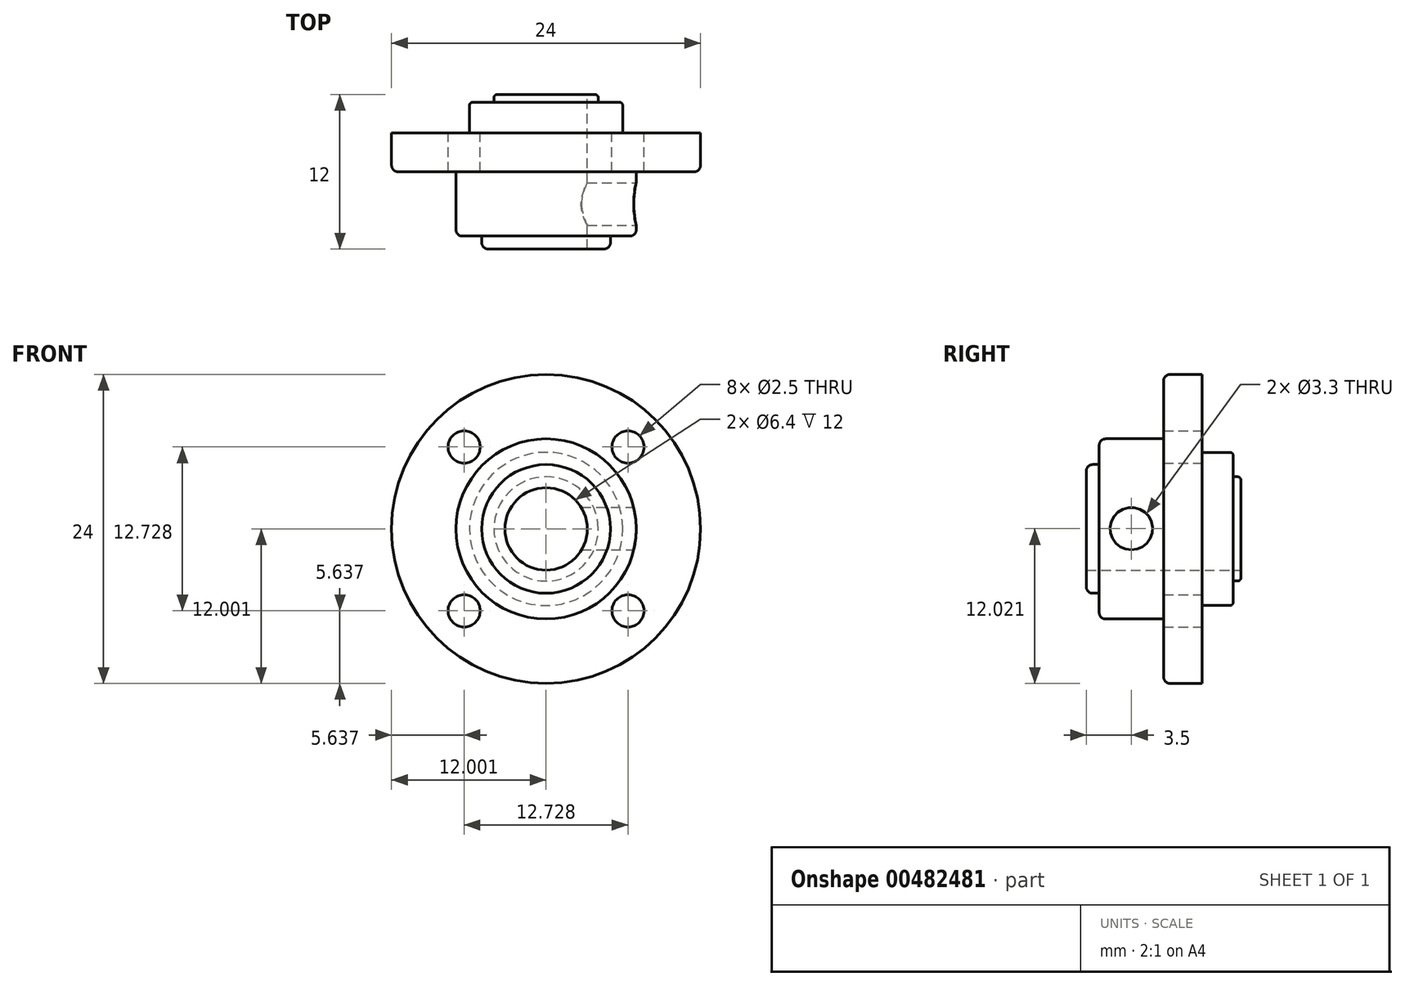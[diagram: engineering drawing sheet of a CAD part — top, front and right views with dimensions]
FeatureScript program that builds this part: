
annotation { "Feature Type Name" : "Feature", "Feature Type Description" : "" }
export const myFeature = defineFeature(function(context is Context, id is Id, definition is map)
    precondition{}
    {
        {
            var Q0;
            Q0=qCreatedBy(makeId("Front.planeOp"),FACE);
            var sketch = newSketch(context, id + "F0", { "sketchPlane" : qUnion([Q0])});
            skCircle(sketch, "E0", {"center": v(-51.93, 29.55) * mm, "radius": 5.95 * mm});
            skCircle(sketch, "E1", {"center": v(-51.93, 29.55) * mm, "radius": 12 * mm});
            skCircle(sketch, "E2", {"center": v(-51.93, 29.55) * mm, "radius": 3.2 * mm});
            skCircle(sketch, "E3", {"center": v(-58.3, 35.91) * mm, "radius": 1.25 * mm});
            skCircle(sketch, "E4", {"center": v(-45.57, 35.91) * mm, "radius": 1.25 * mm});
            skCircle(sketch, "E5", {"center": v(-45.57, 23.19) * mm, "radius": 1.25 * mm});
            skCircle(sketch, "E6", {"center": v(-58.3, 23.19) * mm, "radius": 1.25 * mm});
            skSolve(sketch);
        }
        {
            var Q0;
            Q0 = qSketchRegion(id + "F0", true);
            var Q1;
            Q1=makeQuery(id+"F0.imprint","IMPRINT",FACE,{"disambiguationData":[TD([[makeQuery(id+"F0.imprint","IMPRINT",EDGE,{"derivedFrom":sQuery(id+"F0.wireOp",EDGE,"E0")}),1.0]])]});
            extrude(context, id + "F1", {"entities" : qUnion([Q0, Q1]), "depth" : 3 * mm, "offsetDistance" : 25 * mm});
        }
        {
            var Q0;
            Q0=makeQuery(id+"F1.opExtrude","CAP_FACE",FACE,{"disambiguationData":[OSD([sQuery(id+"F0.wireOp",EDGE,"E1"),sQuery(id+"F0.wireOp",EDGE,"EYXUTqH9-eEcY-GaFt-dMka-iERJke81kBaa"),sQuery(id+"F0.wireOp",EDGE,"KlKgwLJu-OTFO-AsjK-VSUq-wluYezLKTBxm"),sQuery(id+"F0.wireOp",EDGE,"UiC2e6AT-jG4o-S1pj-5Rfj-m6z0H2r1u7PO"),sQuery(id+"F0.wireOp",EDGE,"hBQAIbmH-Tyc7-gpv5-7lbM-7KSF0jIbfKj2"),sQuery(id+"F0.wireOp",EDGE,"E2")])],"isStart":true});
            var sketch = newSketch(context, id + "F2", { "sketchPlane" : qUnion([Q0])});
            skCircle(sketch, "E7", {"center": v(51.93, 29.55) * mm, "radius": 5.95 * mm});
            skSolve(sketch);
        }
        {
            var Q0;
            Q0=makeQuery(id+"F2.imprint","IMPRINT",FACE,{"disambiguationData":[TD([[makeQuery(id+"F2.imprint","IMPRINT",EDGE,{"derivedFrom":sQuery(id+"F2.wireOp",EDGE,"E7")}),1.0]])]});
            extrude(context, id + "F3", {"entities" : qUnion([Q0]), "operationType" : NewBodyOperationType.ADD, "depth" : 2.4 * mm, "offsetDistance" : 25 * mm});
        }
        {
            var Q0;
            Q0=makeQuery(id+"F3.opExtrude","CAP_FACE",FACE,{"disambiguationData":[OSD([sQuery(id+"F0.wireOp",EDGE,"E2"),sQuery(id+"F2.wireOp",EDGE,"E7")])],"isStart":false});
            var sketch = newSketch(context, id + "F4", { "sketchPlane" : qUnion([Q0])});
            skCircle(sketch, "E8", {"center": v(51.93, 29.55) * mm, "radius": 4.05 * mm});
            skSolve(sketch);
        }
        {
            var Q0;
            Q0=makeQuery(id+"F4.imprint","IMPRINT",FACE,{"disambiguationData":[TD([[makeQuery(id+"F4.imprint","IMPRINT",EDGE,{"derivedFrom":sQuery(id+"F4.wireOp",EDGE,"E8")}),1.0]])]});
            extrude(context, id + "F5", {"entities" : qUnion([Q0]), "operationType" : NewBodyOperationType.ADD, "depth" : .6 * mm, "offsetDistance" : 25 * mm});
        }
        {
            var Q0;
            Q0=makeQuery(id+"F1.opExtrude","CAP_FACE",FACE,{"disambiguationData":[OSD([sQuery(id+"F0.wireOp",EDGE,"E1"),sQuery(id+"F0.wireOp",EDGE,"EYXUTqH9-eEcY-GaFt-dMka-iERJke81kBaa"),sQuery(id+"F0.wireOp",EDGE,"KlKgwLJu-OTFO-AsjK-VSUq-wluYezLKTBxm"),sQuery(id+"F0.wireOp",EDGE,"UiC2e6AT-jG4o-S1pj-5Rfj-m6z0H2r1u7PO"),sQuery(id+"F0.wireOp",EDGE,"hBQAIbmH-Tyc7-gpv5-7lbM-7KSF0jIbfKj2"),sQuery(id+"F0.wireOp",EDGE,"E2")])],"isStart":false});
            var sketch = newSketch(context, id + "F6", { "sketchPlane" : qUnion([Q0])});
            skCircle(sketch, "E9", {"center": v(-51.93, 29.55) * mm, "radius": 7 * mm});
            skSolve(sketch);
        }
        {
            var Q0;
            Q0=makeQuery(id+"F6.imprint","IMPRINT",FACE,{"disambiguationData":[TD([[makeQuery(id+"F6.imprint","IMPRINT",EDGE,{"derivedFrom":makeQuery(id+"F1.opExtrude","CAP_EDGE",EDGE,{"disambiguationData":[OSD([sQuery(id+"F0.wireOp",EDGE,"E2")])],"isStart":false})}),-1.0]])]});
            extrude(context, id + "F7", {"entities" : qUnion([Q0]), "operationType" : NewBodyOperationType.ADD, "depth" : 5 * mm, "offsetDistance" : 25 * mm});
        }
        {
            var Q0;
            Q0=qCreatedBy(makeId("Right.planeOp"),FACE);
            var sketch = newSketch(context, id + "F8", { "sketchPlane" : qUnion([Q0])});
            skLineSegment(sketch, "E10", {"start": v(-5.5, 37.57) * mm, "end": v(-5.5, 21.57) * mm, "construction": true});
            skPoint(sketch, "E11", {"position": v(-5.5, 29.57) * mm});
            skCircle(sketch, "E12", {"center": v(-5.5, 29.57) * mm, "radius": 1.65 * mm});
            skSolve(sketch);
        }
        {
            var Q0;
            Q0=makeQuery(id+"F8.imprint","IMPRINT",FACE,{"disambiguationData":[TD([[makeQuery(id+"F8.imprint","IMPRINT",EDGE,{"derivedFrom":sQuery(id+"F8.wireOp",EDGE,"E12")}),1.0]])]});
            var Q1;
            Q1=sQuery(id+"F8.wireOp",EDGE,"E12");
            extrude(context, id + "F9", {"entities" : qUnion([Q0]), "operationType" : NewBodyOperationType.REMOVE, "surfaceEntities" : qUnion([Q1]), "oppositeDirection" : true, "depth" : 50 * mm, "offsetDistance" : 25 * mm});
        }
        {
            var Q0;
            Q0=makeQuery(id+"F7.opExtrude","CAP_EDGE",EDGE,{"disambiguationData":[OSD([sQuery(id+"F6.wireOp",EDGE,"E9")])],"isStart":false});
            var Q1;
            Q1=makeQuery(id+"F1.opExtrude","CAP_EDGE",EDGE,{"disambiguationData":[OSD([sQuery(id+"F0.wireOp",EDGE,"E1")])],"isStart":false});
            var Q2;
            {var subQ0=sQuery(id+"F0.wireOp",EDGE,"E5");var subQ1=sQuery(id+"F0.wireOp",EDGE,"E4");var subQ2=sQuery(id+"F6.wireOp",EDGE,"E9");Q2=makeQuery(id+"F7.boolean.opBoolean","SPLIT",EDGE,{"disambiguationData":[TD([makeQuery(id+"F1.opExtrude","CAP_FACE",FACE,{"disambiguationData":[OSD([sQuery(id+"F0.wireOp",EDGE,"E1"),sQuery(id+"F0.wireOp",EDGE,"E2"),sQuery(id+"F0.wireOp",EDGE,"E3"),subQ1,subQ0,sQuery(id+"F0.wireOp",EDGE,"E6")])],"isStart":false}),makeQuery(id+"F1.opExtrude","SWEPT_FACE",FACE,{"disambiguationData":[OSD([subQ1])]}),makeQuery(id+"F1.opExtrude","SWEPT_FACE",FACE,{"disambiguationData":[OSD([subQ0])]}),makeQuery(id+"F7.opExtrude","SWEPT_FACE",FACE,{"disambiguationData":[OSD([subQ2])]})])],"derivedFrom":makeQuery(id+"F7.opExtrude","CAP_EDGE",EDGE,{"disambiguationData":[OSD([subQ2])],"isStart":true})});}
            fillet(context, id + "F10", {"entities" : qUnion([Q0, Q1, Q2]), "radius" : .5 * mm, "tangentPropagation" : true, "allowEdgeOverflow" : false});
        }
        {
            var Q0;
            Q0=makeQuery(id+"F5.opExtrude","CAP_EDGE",EDGE,{"disambiguationData":[OSD([sQuery(id+"F4.wireOp",EDGE,"E8")])],"isStart":false});
            var Q1;
            Q1=makeQuery(id+"F3.opExtrude","CAP_EDGE",EDGE,{"disambiguationData":[OSD([sQuery(id+"F2.wireOp",EDGE,"E7")])],"isStart":false});
            fillet(context, id + "F11", {"entities" : qUnion([Q0, Q1]), "radius" : .25 * mm, "tangentPropagation" : true, "allowEdgeOverflow" : false});
        }
        {
            var Q0;
            Q0=makeQuery(id+"F7.opExtrude","CAP_FACE",FACE,{"disambiguationData":[OSD([sQuery(id+"F0.wireOp",EDGE,"E2"),sQuery(id+"F6.wireOp",EDGE,"E9")])],"isStart":false});
            var sketch = newSketch(context, id + "F12", { "sketchPlane" : qUnion([Q0])});
            skCircle(sketch, "E13", {"center": v(-51.93, 29.55) * mm, "radius": 5 * mm});
            skSolve(sketch);
        }
        {
            var Q0;
            Q0=makeQuery(id+"F12.imprint","IMPRINT",FACE,{"disambiguationData":[TD([[makeQuery(id+"F12.imprint","IMPRINT",EDGE,{"derivedFrom":sQuery(id+"F12.wireOp",EDGE,"E13")}),1.0]])]});
            extrude(context, id + "F13", {"entities" : qUnion([Q0]), "operationType" : NewBodyOperationType.ADD, "depth" : 1 * mm, "offsetDistance" : 25 * mm});
        }
        {
            var Q0;
            Q0=makeQuery(id+"F13.opExtrude","CAP_EDGE",EDGE,{"disambiguationData":[OSD([sQuery(id+"F12.wireOp",EDGE,"E13")])],"isStart":false});
            fillet(context, id + "F14", {"entities" : qUnion([Q0]), "radius" : .5 * mm, "tangentPropagation" : true, "allowEdgeOverflow" : false});
        }
        {
            var Q0;
            Q0=makeQuery(id+"F1.opExtrude","SWEPT_BODY",BODY,{"disambiguationData":[OSD([sQuery(id+"F0.wireOp",EDGE,"E1"),sQuery(id+"F0.wireOp",EDGE,"E2"),sQuery(id+"F0.wireOp",EDGE,"E3"),sQuery(id+"F0.wireOp",EDGE,"E4"),sQuery(id+"F0.wireOp",EDGE,"E5"),sQuery(id+"F0.wireOp",EDGE,"E6")])]});
            transform(context, id + "F15", {"entities" : qUnion([Q0]), "transformType" : TransformType.TRANSLATION_3D, "dx" : 0 * mm, "dy" : 0 * mm, "dz" : 0 * mm, "makeCopy" : true});
        }
    });
